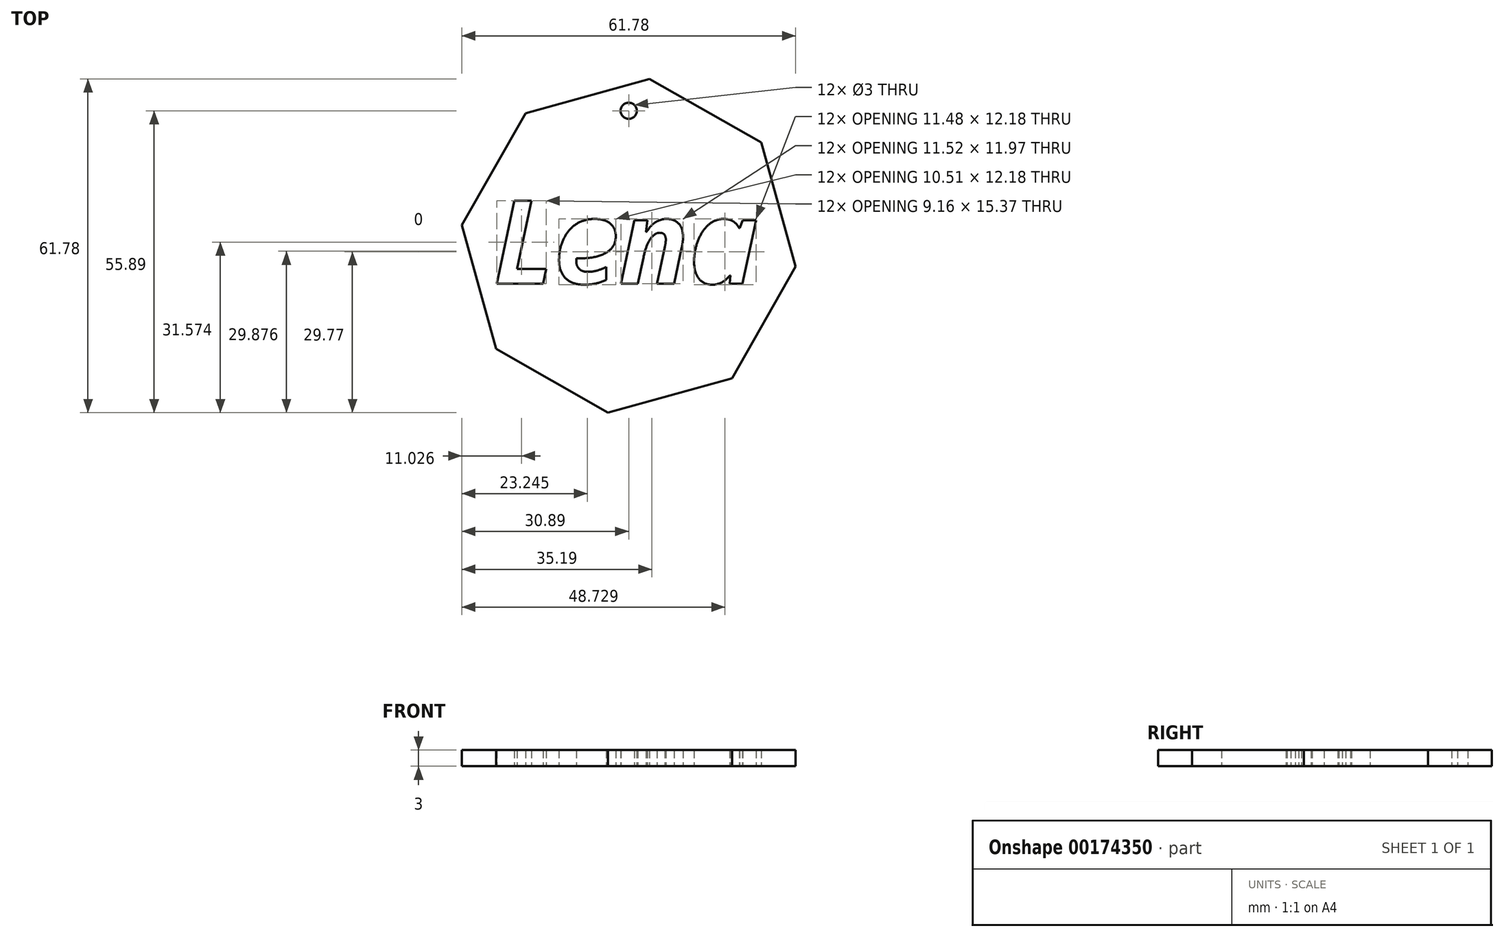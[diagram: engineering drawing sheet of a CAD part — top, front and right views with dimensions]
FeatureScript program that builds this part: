
annotation { "Feature Type Name" : "Feature", "Feature Type Description" : "" }
export const myFeature = defineFeature(function(context is Context, id is Id, definition is map)
    precondition{}
    {
        {
            var Q0;
            Q0=qCreatedBy(makeId("Top.planeOp"),FACE);
            var sketch = newSketch(context, id + "F0", { "sketchPlane" : qUnion([Q0])});
            skText(sketch, "E0", { "text": "Maia", "fontName": "Arimo-Bold.ttf"});
            skLineSegment(sketch, "E1.bottom", {"start": v(-30, 23) * mm, "end": v(30, 23) * mm});
            skLineSegment(sketch, "E1.top", {"start": v(-30, -7) * mm, "end": v(30, -7) * mm});
            skLineSegment(sketch, "E1.left", {"start": v(-35, 18) * mm, "end": v(-35, -2) * mm});
            skLineSegment(sketch, "E1.right", {"start": v(35, 18) * mm, "end": v(35, -2) * mm});
            skCircle(sketch, "E2", {"center": v(-4, 19) * mm, "radius": 1.5 * mm});
            skCircle(sketch, "E3.MirrorC", {"center": v(4, 19) * mm, "radius": 1.5 * mm});
            skPoint(sketch, "E4.visualSharp", {"position": v(-35, 23) * mm});
            skArc(sketch, "E4.filletArc", {"start": v(-30, 23) * mm, "mid": v(-33.54, 21.54) * mm, "end": v(-35, 18) * mm});
            skPoint(sketch, "E5.visualSharp", {"position": v(-35, -7) * mm});
            skArc(sketch, "E5.filletArc", {"start": v(-35, -2) * mm, "mid": v(-33.54, -5.54) * mm, "end": v(-30, -7) * mm});
            skPoint(sketch, "E6.visualSharp", {"position": v(35, 23) * mm});
            skArc(sketch, "E6.filletArc", {"start": v(35, 18) * mm, "mid": v(33.54, 21.54) * mm, "end": v(30, 23) * mm});
            skPoint(sketch, "E7.visualSharp", {"position": v(35, -7) * mm});
            skArc(sketch, "E7.filletArc", {"start": v(30, -7) * mm, "mid": v(33.54, -5.54) * mm, "end": v(35, -2) * mm});
            const initialGuessF0  = {"E0": [-0.025, 0, 1, 0, 0.01566]};
            skSetInitialGuess(sketch, initialGuessF0);
            skSolve(sketch);
        }
        {
            var Q0;
            Q0=qCreatedBy(makeId("Top.planeOp"),FACE);
            var sketch = newSketch(context, id + "F1", { "sketchPlane" : qUnion([Q0])});
            skText(sketch, "E8", { "text": "Lena", "fontName": "OpenSans-BoldItalic.ttf"});
            skCircle(sketch, "E9.cCircle", {"center": v(0, 0) * mm, "radius": 28.76 * mm, "construction": true});
            skLineSegment(sketch, "E9.0", {"start": v(30.89, -3.86) * mm, "end": v(19.11, -24.57) * mm});
            skLineSegment(sketch, "E9.1", {"start": v(19.11, -24.57) * mm, "end": v(-3.86, -30.89) * mm});
            skLineSegment(sketch, "E9.2", {"start": v(-3.86, -30.89) * mm, "end": v(-24.57, -19.11) * mm});
            skLineSegment(sketch, "E9.3", {"start": v(-24.57, -19.11) * mm, "end": v(-30.89, 3.86) * mm});
            skLineSegment(sketch, "E9.4", {"start": v(-30.89, 3.86) * mm, "end": v(-19.11, 24.57) * mm});
            skLineSegment(sketch, "E9.5", {"start": v(-19.11, 24.57) * mm, "end": v(3.86, 30.89) * mm});
            skLineSegment(sketch, "E9.6", {"start": v(3.86, 30.89) * mm, "end": v(24.57, 19.11) * mm});
            skLineSegment(sketch, "E9.7", {"start": v(24.57, 19.11) * mm, "end": v(30.89, -3.86) * mm});
            skPoint(sketch, "E9.0.midPoint", {"position": v(25, -14.21) * mm});
            skCircle(sketch, "E10", {"center": v(0, 25) * mm, "radius": 1.5 * mm});
            const initialGuessF1  = {"E8": [-0.025, -0.007, 1, 0, 0.0155]};
            skSetInitialGuess(sketch, initialGuessF1);
            skSolve(sketch);
        }
        {
            var Q0;
            Q0 = qSketchRegion(id + "F1", true);
            extrude(context, id + "F2", {"entities" : qUnion([Q0]), "depth" : 3 * mm});
        }
    });
